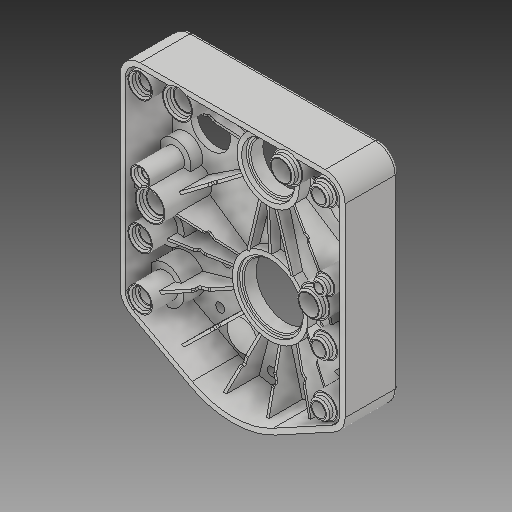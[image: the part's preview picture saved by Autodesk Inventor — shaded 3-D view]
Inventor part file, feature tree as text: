
AUTODESK INVENTOR PART (.ipt)
format: ipt  version: 2017 (Build 210142000, 142)  size: 887,296 bytes
history: native  units: in
note: dims shown in document units (in); Inventor stores cm internally (conversion verified against a paired STEP export)
features: fillet x1
ambient origin geometry x8: Origin, YZ Plane, XZ Plane, XY Plane, X Axis, Y Axis, Z Axis, Center Point
bodies: Solid1 (feature_tree)
feature tree (1):
  fillet  "Fillet18"  [1 undecoded]
note: 1 required parameter value undecoded (feature->parameter linkage not recoverable at this tier; creation-order binding heuristic only, values carry confidence <= 0.55)
